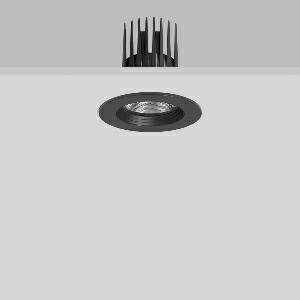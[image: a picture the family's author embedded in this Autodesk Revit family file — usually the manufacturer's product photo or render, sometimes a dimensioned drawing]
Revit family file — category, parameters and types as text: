
# Revit family: heledon_mini_e_901748_003_1_123b
name_source: partatom
category: Lighting Fixtures
units: mm (PartAtom-declared; Revit-internal decimal feet)

## family parameters
Cut with Voids When Loaded = No
Host = Face
Light Source = No
Part Type = Normal
Room Calculation Point = No
Round Connector Dimension = Use Diameter
Shared = No

## types (1)
- HELEDON mini E (1 x LED Modul 940, 3800 lm, 4000)
    Apparent Load = 29 VA
    Approval mark = CE
    CIE Flux Codes = 100 100 100 100 100
    Color Rendering = 92
    Color Temperature = 4000
    Default Elevation = 1800 mm
    Description = Series: HELEDON mini
Round recessed downlight. Housing: die-cast aluminium, powder-coated. Black plastic ring and recessed LED to prevent glare from the side. Optical assembly with reflector made of MIRO-Silver with 98% total light reflection for outstanding efficiency - can be changed without tools. Best colour rendering index Ra>90. Suitable for Recessed ceiling mounting. Installation without tools thanks to spring fastening system. Including separate LED converter with connecting cable 600 mm.High quality converter without flickering and stroboscopic effect. Through-wiring box (5 pole) available as accessory. The following accessories can be mounted without use of tools: interchangeable lenses, decorative glasses, honeycomb louvre, clear and frosted diffusers, white interchangeable plastic ring. 
Colour: deep black, matt (RAL 9005)
Diameter: 124 mm
Height: 3 mm
Cut-out diameter: 114 mm
Recess height: 170 mm
Luminaire: recess height: 120 mm
Lamp: LED
Socket: without socket
Colour temperature: 4000K
Colour rendering index (CRI): 92
System power: 29 W
Rated luminous flux: 3800 lm
Luminous efficiency: 131 lm/W
Control gear: Regulated power supply
Protection class: II
Type of protection: IP 20
    Height = 0 mm  [stored 0 ft]
    Lamp = 1 x LED Modul 940
    Lamp Light Flux = 3800 lm
    Lamp count = 1
    Length = 124 mm  [stored 0.406824 ft]
    Lifetime = 50000 h
    Luminous efficacy = 131 lm/W
    Manufacturer = RZB
    ModVariant = No
    Model = 901748.003.1
    Mounting Place = Ceiling
    Mounting Type = Recessed
    Number of Poles = 1
    OnlyDefault = Yes
    Power Factor = 1
    Product Name = HELEDON mini E
    Product group = Recessed downlights
    ProductGroupID = 402
    Protection Class = Protection class II
    Protection Degree = IP 20
    RLX_Detail_Level = 1
    RLX_Emergency_Light_Flux = 0 lm
    RLX_Emergency_Type = 0
    RLX_Emergency_Type_DB = No
    RlxData = <blob elided: 125797 chars, md5=93a68cd2>
    Socket = socket
    Standby Power = 0 W
    System Light Flux = 3800 lm
    System Power = 29 W
    Type Comments = Product without accessories
    Type Image = 901657.003.jpg
    URL = http://relux.com
    VarID = ---
    Voltage = 230 V
    Voltage Range = 220-240 V
    Weight = 0.00 kg
    Width = 0 mm  [stored 0 ft]

note: [stored X ft] marks values corroborated as IEEE doubles in the binary element streams (Revit-internal decimal feet)

## geometry (parser evidence)
native form markers: Blend x4, Sweep x12
no freeform markers — native parametric forms only
